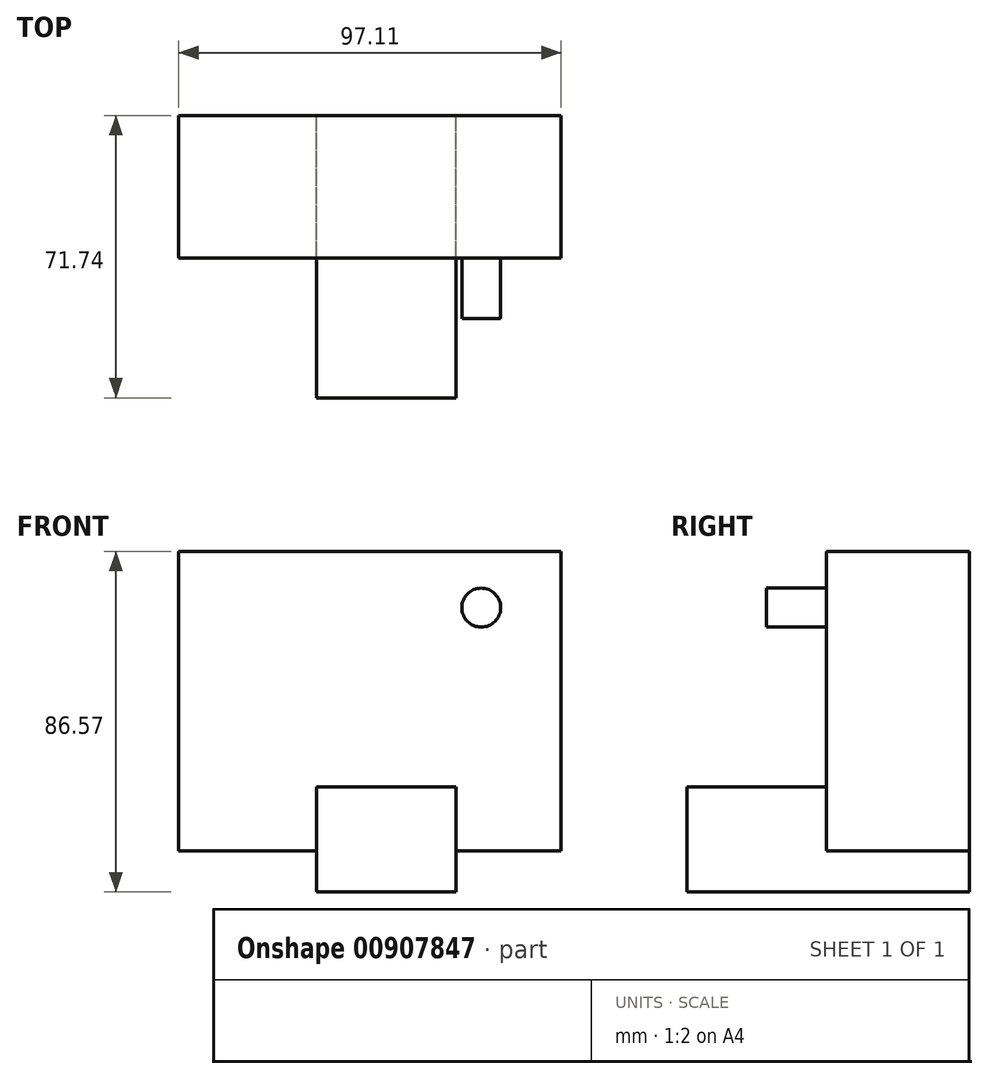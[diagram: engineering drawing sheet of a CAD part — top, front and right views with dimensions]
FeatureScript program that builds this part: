
annotation { "Feature Type Name" : "Feature", "Feature Type Description" : "" }
export const myFeature = defineFeature(function(context is Context, id is Id, definition is map)
    precondition{}
    {
        {
            var Q0;
            Q0=qCreatedBy(makeId("Front.planeOp"),FACE);
            var sketch = newSketch(context, id + "F0", { "sketchPlane" : qUnion([Q0])});
            skLineSegment(sketch, "E0.bottom", {"start": v(-42.37, 31.84) * mm, "end": v(54.74, 31.84) * mm});
            skLineSegment(sketch, "E0.top", {"start": v(-42.37, -44.33) * mm, "end": v(54.74, -44.33) * mm});
            skLineSegment(sketch, "E0.left", {"start": v(-42.37, 31.84) * mm, "end": v(-42.37, -44.33) * mm});
            skLineSegment(sketch, "E0.right", {"start": v(54.74, 31.84) * mm, "end": v(54.74, -44.33) * mm});
            skSolve(sketch);
        }
        {
            var Q0;
            Q0=makeQuery(id+"F0.imprint","IMPRINT",FACE,{"disambiguationData":[TD([[makeQuery(id+"F0.imprint","IMPRINT",EDGE,{"derivedFrom":sQuery(id+"F0.wireOp",EDGE,"E0.bottom")}),-1.0]])]});
            extrude(context, id + "F1", {"entities" : qUnion([Q0]), "depth" : 36.3 * mm, "offsetDistance" : 25.4 * mm});
        }
        {
            var Q0;
            Q0=qCreatedBy(makeId("Front.planeOp"),FACE);
            var sketch = newSketch(context, id + "F2", { "sketchPlane" : qUnion([Q0])});
            skCircle(sketch, "E1", {"center": v(34.46, 17.54) * mm, "radius": 4.95 * mm});
            skPoint(sketch, "E1.first.point", {"position": v(39.35, 18.27) * mm});
            skPoint(sketch, "E1.second.point", {"position": v(32.7, 12.9) * mm});
            skPoint(sketch, "E1.third.point", {"position": v(32.17, 21.92) * mm});
            skSolve(sketch);
        }
        {
            var Q0;
            Q0 = qSketchRegion(id + "F2", true);
            extrude(context, id + "F3", {"entities" : qUnion([Q0]), "operationType" : NewBodyOperationType.ADD, "depth" : 51.58 * mm, "offsetDistance" : 25.4 * mm});
        }
        {
            var Q0;
            Q0=qCreatedBy(makeId("Front.planeOp"),FACE);
            var sketch = newSketch(context, id + "F4", { "sketchPlane" : qUnion([Q0])});
            skLineSegment(sketch, "E2.bottom", {"start": v(-7.4, -28.03) * mm, "end": v(28.05, -28.03) * mm});
            skLineSegment(sketch, "E2.top", {"start": v(-7.4, -54.73) * mm, "end": v(28.05, -54.73) * mm});
            skLineSegment(sketch, "E2.left", {"start": v(-7.4, -28.03) * mm, "end": v(-7.4, -54.73) * mm});
            skLineSegment(sketch, "E2.right", {"start": v(28.05, -28.03) * mm, "end": v(28.05, -54.73) * mm});
            skSolve(sketch);
        }
        {
            var Q0;
            Q0 = qSketchRegion(id + "F4", true);
            extrude(context, id + "F5", {"entities" : qUnion([Q0]), "operationType" : NewBodyOperationType.ADD, "depth" : 71.74 * mm, "offsetDistance" : 25.4 * mm});
        }
    });
